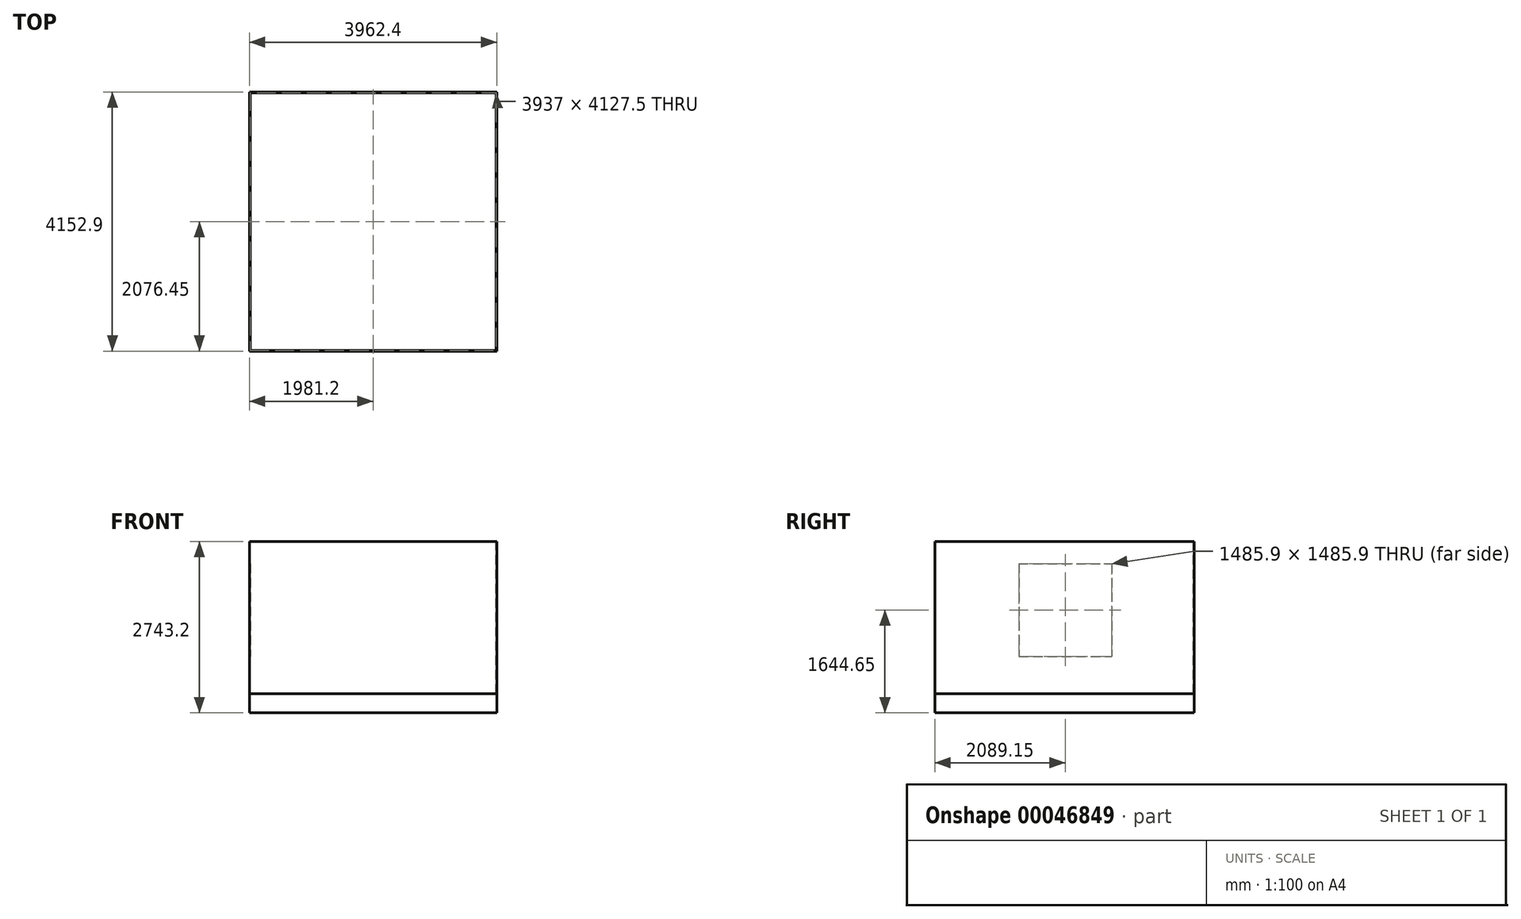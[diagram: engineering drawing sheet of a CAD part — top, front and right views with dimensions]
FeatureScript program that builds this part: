
annotation { "Feature Type Name" : "Feature", "Feature Type Description" : "" }
export const myFeature = defineFeature(function(context is Context, id is Id, definition is map)
    precondition{}
    {
        {
            var Q0;
            Q0=qCreatedBy(makeId("Right.planeOp"),FACE);
            cPlane(context, id + "F0", {"entities" : qUnion([Q0]), "cplaneType" : CPlaneType.OFFSET, "offset" : 3962.4 * mm, "width" : 152.4 * mm, "height" : 152.4 * mm});
        }
        {
            var Q0;
            Q0=qCreatedBy(makeId("Front.planeOp"),FACE);
            cPlane(context, id + "F1", {"entities" : qUnion([Q0]), "cplaneType" : CPlaneType.OFFSET, "offset" : 4152.9 * mm, "oppositeDirection" : true, "width" : 152.4 * mm, "height" : 152.4 * mm});
        }
        {
            var Q0;
            Q0=qCreatedBy(makeId("Top.planeOp"),FACE);
            var sketch = newSketch(context, id + "F2", { "sketchPlane" : qUnion([Q0])});
            skLineSegment(sketch, "E0.bottom", {"start": v(0, 0) * mm, "end": v(3962.4, 0) * mm});
            skLineSegment(sketch, "E0.top", {"start": v(0, 4152.9) * mm, "end": v(3962.4, 4152.9) * mm});
            skLineSegment(sketch, "E0.left", {"start": v(0, 0) * mm, "end": v(0, 4152.9) * mm});
            skLineSegment(sketch, "E0.right", {"start": v(3962.4, 0) * mm, "end": v(3962.4, 4152.9) * mm});
            skSolve(sketch);
        }
        {
            var Q0;
            Q0=qSketchRegion(id+"F2",true);
            extrude(context, id + "F3", {"entities" : qUnion([Q0]), "oppositeDirection" : true, "depth" : 304.8 * mm});
        }
        {
            var Q0;
            Q0=qSketchRegion(id+"F2",true);
            extrude(context, id + "F4", {"entities" : qUnion([Q0]), "depth" : 2438.4 * mm});
        }
        {
            var Q0;
            Q0=makeQuery(id+"F4.opExtrude","CAP_FACE",FACE,{"disambiguationData":[OSD([sQuery(id+"F2.wireOp",EDGE,"E0.bottom"),sQuery(id+"F2.wireOp",EDGE,"E0.top"),sQuery(id+"F2.wireOp",EDGE,"E0.left"),sQuery(id+"F2.wireOp",EDGE,"E0.right")])],"isStart":false});
            var sketch = newSketch(context, id + "F5", { "sketchPlane" : qUnion([Q0])});
            skLineSegment(sketch, "E1.0", {"start": v(12.7, 12.7) * mm, "end": v(12.7, 4140.2) * mm});
            skLineSegment(sketch, "E1.1", {"start": v(12.7, 12.7) * mm, "end": v(3949.7, 12.7) * mm});
            skLineSegment(sketch, "E1.2", {"start": v(3949.7, 12.7) * mm, "end": v(3949.7, 4140.2) * mm});
            skLineSegment(sketch, "E1.3", {"start": v(12.7, 4140.2) * mm, "end": v(3949.7, 4140.2) * mm});
            skSolve(sketch);
        }
        {
            var Q0;
            Q0=qSketchRegion(id+"F5",true);
            var Q1;
            Q1=qCreatedBy(makeId("Top.planeOp"),FACE);
            extrude(context, id + "F6", {"entities" : qUnion([Q0]), "operationType" : NewBodyOperationType.REMOVE, "endBound" : BoundingType.UP_TO_SURFACE, "oppositeDirection" : true, "endBoundEntityFace" : qUnion([Q1]), "depth" : 30.48 * mm});
        }
        {
            var Q0;
            Q0=makeQuery(id+"F6.boolean.opBoolean","COPY",FACE,{"derivedFrom":makeQuery(id+"F6.opExtrude","SWEPT_FACE",FACE,{"disambiguationData":[OSD([sQuery(id+"F5.wireOp",EDGE,"E1.0")])]})});
            var sketch = newSketch(context, id + "F7", { "sketchPlane" : qUnion([Q0])});
            skLineSegment(sketch, "E2.bottom", {"start": v(1346.2, 2082.8) * mm, "end": v(2832.1, 2082.8) * mm});
            skLineSegment(sketch, "E2.top", {"start": v(1346.2, 596.9) * mm, "end": v(2832.1, 596.9) * mm});
            skLineSegment(sketch, "E2.left", {"start": v(1346.2, 2082.8) * mm, "end": v(1346.2, 596.9) * mm});
            skLineSegment(sketch, "E2.right", {"start": v(2832.1, 2082.8) * mm, "end": v(2832.1, 596.9) * mm});
            skSolve(sketch);
        }
        {
            var Q0;
            Q0=qSketchRegion(id+"F7",true);
            extrude(context, id + "F8", {"entities" : qUnion([Q0]), "operationType" : NewBodyOperationType.REMOVE, "endBound" : BoundingType.UP_TO_NEXT, "oppositeDirection" : true, "depth" : 25.4 * mm});
        }
    });
